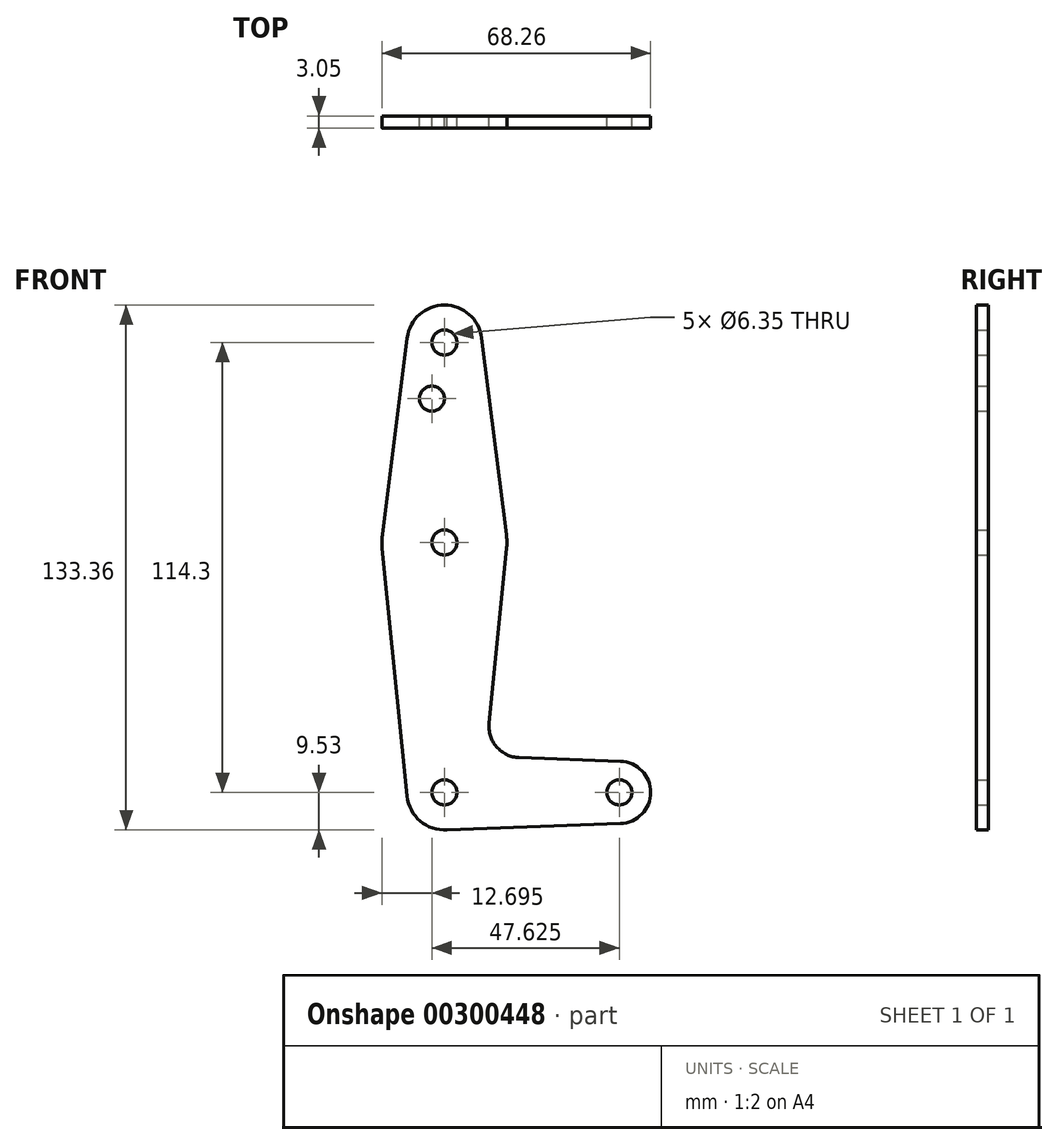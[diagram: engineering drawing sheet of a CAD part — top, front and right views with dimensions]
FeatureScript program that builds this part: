
annotation { "Feature Type Name" : "Feature", "Feature Type Description" : "" }
export const myFeature = defineFeature(function(context is Context, id is Id, definition is map)
    precondition{}
    {
        {
            var Q0;
            Q0=qCreatedBy(makeId("Front.planeOp"),FACE);
            var sketch = newSketch(context, id + "F0", { "sketchPlane" : qUnion([Q0])});
            skLineSegment(sketch, "E0", {"start": v(0, 0) * mm, "end": v(0, 114.3) * mm, "construction": true});
            skLineSegment(sketch, "E1", {"start": v(0, 0) * mm, "end": v(44.45, 0) * mm, "construction": true});
            skCircle(sketch, "E2", {"center": v(0, 0) * mm, "radius": 9.53 * mm});
            skCircle(sketch, "E3", {"center": v(0, 63.5) * mm, "radius": 15.88 * mm});
            skCircle(sketch, "E4", {"center": v(0, 114.3) * mm, "radius": 9.53 * mm});
            skCircle(sketch, "E5", {"center": v(44.45, 0) * mm, "radius": 7.94 * mm});
            skLineSegment(sketch, "E6", {"start": v(15.8, 61.91) * mm, "end": v(11.34, 17.59) * mm});
            skLineSegment(sketch, "E7", {"start": v(-9.45, 115.5) * mm, "end": v(-15.75, 65.48) * mm});
            skLineSegment(sketch, "E8", {"start": v(9.45, 115.5) * mm, "end": v(15.75, 65.48) * mm});
            skLineSegment(sketch, "E9", {"start": v(-15.8, 61.91) * mm, "end": v(-9.48, -0.95) * mm});
            skLineSegment(sketch, "E10", {"start": v(18.97, 8.85) * mm, "end": v(44.73, 7.93) * mm});
            skLineSegment(sketch, "E11", {"start": v(0, -9.53) * mm, "end": v(44.73, -7.93) * mm});
            skCircle(sketch, "E12", {"center": v(0, 114.3) * mm, "radius": 3.18 * mm});
            skCircle(sketch, "E13", {"center": v(0, 0) * mm, "radius": 3.18 * mm});
            skCircle(sketch, "E14", {"center": v(44.45, 0) * mm, "radius": 3.18 * mm});
            skCircle(sketch, "E15", {"center": v(0, 63.5) * mm, "radius": 3.18 * mm});
            skCircle(sketch, "E16", {"center": v(-3.18, 100.03) * mm, "radius": 3.18 * mm});
            skArc(sketch, "E17.filletArc", {"start": v(11.34, 17.59) * mm, "mid": v(13.26, 11.57) * mm, "end": v(18.97, 8.85) * mm});
            skSolve(sketch);
        }
        {
            var Q0;
            Q0 = qSketchRegion(id + "F0", true);
            extrude(context, id + "F1", {"entities" : qUnion([Q0]), "depth" : 3.05 * mm});
        }
    });
